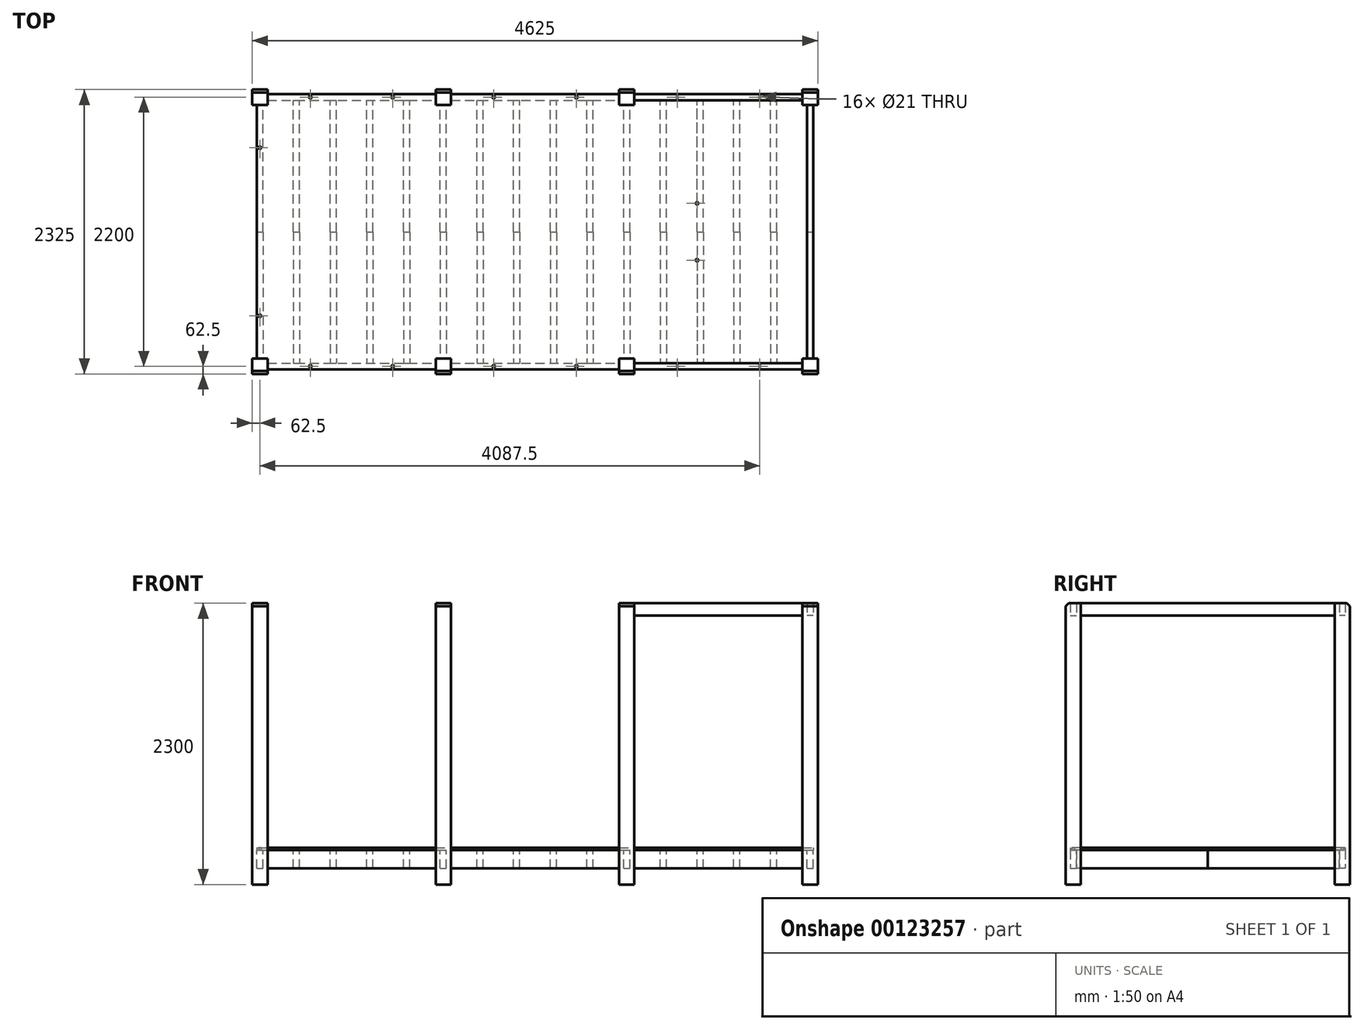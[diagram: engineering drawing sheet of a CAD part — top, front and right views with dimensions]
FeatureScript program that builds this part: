
annotation { "Feature Type Name" : "Feature", "Feature Type Description" : "" }
export const myFeature = defineFeature(function(context is Context, id is Id, definition is map)
    precondition{}
    {
        {
            var Q0;
            Q0=qCreatedBy(makeId("Front.planeOp"),FACE);
            cPlane(context, id + "F0", {"entities" : qUnion([Q0]), "cplaneType" : CPlaneType.OFFSET, "offset" : 1100 * mm, "width" : 150 * mm, "height" : 150 * mm});
        }
        {
            var Q0;
            Q0=qCreatedBy(id+"F0.planeOp",FACE);
            var sketch = newSketch(context, id + "F1", { "sketchPlane" : qUnion([Q0])});
            skLineSegment(sketch, "E0.bottom", {"start": v(-2312.5, 951.35) * mm, "end": v(-2187.5, 951.35) * mm});
            skLineSegment(sketch, "E0.top", {"start": v(-2312.5, -1348.65) * mm, "end": v(-2187.5, -1348.65) * mm});
            skLineSegment(sketch, "E0.left", {"start": v(-2312.5, 951.35) * mm, "end": v(-2312.5, -1348.65) * mm});
            skLineSegment(sketch, "E0.right", {"start": v(-2187.5, 951.35) * mm, "end": v(-2187.5, -1348.65) * mm});
            skLineSegment(sketch, "E1.direction1", {"start": v(-2312.5, -1348.65) * mm, "end": v(-812.5, -1348.65) * mm, "construction": true});
            skLineSegment(sketch, "E2.1.0.0", {"start": v(-812.5, 951.35) * mm, "end": v(-812.5, -1348.65) * mm});
            skLineSegment(sketch, "E2.1.0.1", {"start": v(-812.5, 951.35) * mm, "end": v(-687.5, 951.35) * mm});
            skLineSegment(sketch, "E2.1.0.2", {"start": v(-687.5, 951.35) * mm, "end": v(-687.5, -1348.65) * mm});
            skLineSegment(sketch, "E2.2.0.0", {"start": v(687.5, 951.35) * mm, "end": v(687.5, -1348.65) * mm});
            skLineSegment(sketch, "E2.2.0.1", {"start": v(687.5, 951.35) * mm, "end": v(812.5, 951.35) * mm});
            skLineSegment(sketch, "E2.2.0.2", {"start": v(812.5, 951.35) * mm, "end": v(812.5, -1348.65) * mm});
            skLineSegment(sketch, "E3.0.3.0", {"start": v(2187.5, 951.35) * mm, "end": v(2187.5, -1348.65) * mm});
            skLineSegment(sketch, "E3.3.3.0", {"start": v(2187.5, 951.35) * mm, "end": v(2312.5, 951.35) * mm});
            skLineSegment(sketch, "E3.6.3.0", {"start": v(2312.5, 951.35) * mm, "end": v(2312.5, -1348.65) * mm});
            skLineSegment(sketch, "E4", {"start": v(-812.5, -1348.65) * mm, "end": v(-687.5, -1348.65) * mm});
            skLineSegment(sketch, "E5", {"start": v(687.5, -1348.65) * mm, "end": v(812.5, -1348.65) * mm});
            skLineSegment(sketch, "E6", {"start": v(2187.5, -1348.65) * mm, "end": v(2312.5, -1348.65) * mm});
            skSolve(sketch);
        }
        {
            var Q0;
            Q0=makeQuery(id+"F1.imprint","IMPRINT",FACE,{"disambiguationData":[TD([[makeQuery(id+"F1.imprint","IMPRINT",EDGE,{"derivedFrom":sQuery(id+"F1.wireOp",EDGE,"E0.bottom")}),-1.0]])]});
            var Q1;
            Q1=makeQuery(id+"F1.imprint","IMPRINT",FACE,{"disambiguationData":[TD([[makeQuery(id+"F1.imprint","IMPRINT",EDGE,{"derivedFrom":sQuery(id+"F1.wireOp",EDGE,"E2.1.0.0")}),1.0]])]});
            var Q2;
            Q2=makeQuery(id+"F1.imprint","IMPRINT",FACE,{"disambiguationData":[TD([[makeQuery(id+"F1.imprint","IMPRINT",EDGE,{"derivedFrom":sQuery(id+"F1.wireOp",EDGE,"E2.2.0.0")}),1.0]])]});
            var Q3;
            Q3=makeQuery(id+"F1.imprint","IMPRINT",FACE,{"disambiguationData":[TD([[makeQuery(id+"F1.imprint","IMPRINT",EDGE,{"derivedFrom":sQuery(id+"F1.wireOp",EDGE,"E3.0.3.0")}),1.0]])]});
            extrude(context, id + "F2", {"entities" : qUnion([Q0, Q1, Q2, Q3]), "endBound" : BoundingType.SYMMETRIC, "depth" : 125 * mm});
        }
        {
            var Q0;
            Q0=qCreatedBy(id+"F0.planeOp",FACE);
            var sketch = newSketch(context, id + "F3", { "sketchPlane" : qUnion([Q0])});
            skLineSegment(sketch, "E7.bottom", {"start": v(-2187.5, -1067.65) * mm, "end": v(-812.5, -1067.65) * mm});
            skLineSegment(sketch, "E7.top", {"start": v(-2187.5, -1217.65) * mm, "end": v(-812.5, -1217.65) * mm});
            skLineSegment(sketch, "E7.left", {"start": v(-2187.5, -1067.65) * mm, "end": v(-2187.5, -1217.65) * mm});
            skLineSegment(sketch, "E7.right", {"start": v(-812.5, -1067.65) * mm, "end": v(-812.5, -1217.65) * mm});
            skSolve(sketch);
        }
        {
            var Q0;
            Q0=qCreatedBy(id+"F0.planeOp",FACE);
            var sketch = newSketch(context, id + "F4", { "sketchPlane" : qUnion([Q0])});
            skLineSegment(sketch, "E8.bottom", {"start": v(812.5, -1067.65) * mm, "end": v(2187.5, -1067.65) * mm});
            skLineSegment(sketch, "E8.top", {"start": v(812.5, -1217.65) * mm, "end": v(2187.5, -1217.65) * mm});
            skLineSegment(sketch, "E8.left", {"start": v(812.5, -1067.65) * mm, "end": v(812.5, -1217.65) * mm});
            skLineSegment(sketch, "E8.right", {"start": v(2187.5, -1067.65) * mm, "end": v(2187.5, -1217.65) * mm});
            skLineSegment(sketch, "E9.bottom", {"start": v(-687.5, -1067.65) * mm, "end": v(687.5, -1067.65) * mm});
            skLineSegment(sketch, "E9.top", {"start": v(-687.5, -1217.65) * mm, "end": v(687.5, -1217.65) * mm});
            skLineSegment(sketch, "E9.left", {"start": v(-687.5, -1067.65) * mm, "end": v(-687.5, -1217.65) * mm});
            skLineSegment(sketch, "E9.right", {"start": v(687.5, -1067.65) * mm, "end": v(687.5, -1217.65) * mm});
            skSolve(sketch);
        }
        {
            var Q0;
            Q0=makeQuery(id+"F3.imprint","IMPRINT",FACE,{"disambiguationData":[TD([[makeQuery(id+"F3.imprint","IMPRINT",EDGE,{"derivedFrom":sQuery(id+"F3.wireOp",EDGE,"E7.bottom")}),-1.0]])]});
            var Q1;
            Q1=makeQuery(id+"F4.imprint","IMPRINT",FACE,{"disambiguationData":[TD([[makeQuery(id+"F4.imprint","IMPRINT",EDGE,{"derivedFrom":sQuery(id+"F4.wireOp",EDGE,"E9.bottom")}),-1.0]])]});
            var Q2;
            Q2=makeQuery(id+"F4.imprint","IMPRINT",FACE,{"disambiguationData":[TD([[makeQuery(id+"F4.imprint","IMPRINT",EDGE,{"derivedFrom":sQuery(id+"F4.wireOp",EDGE,"E8.bottom")}),-1.0]])]});
            extrude(context, id + "F5", {"entities" : qUnion([Q0, Q1, Q2]), "endBound" : BoundingType.SYMMETRIC, "depth" : 50 * mm});
        }
        {
            var Q0;
            Q0=qCreatedBy(makeId("Top.planeOp"),FACE);
            cPlane(context, id + "F6", {"entities" : qUnion([Q0]), "cplaneType" : CPlaneType.OFFSET, "offset" : 1067.65 * mm, "oppositeDirection" : true, "width" : 150 * mm, "height" : 150 * mm});
        }
        {
            var Q0;
            Q0=qCreatedBy(id+"F6.planeOp",FACE);
            var sketch = newSketch(context, id + "F7", { "sketchPlane" : qUnion([Q0])});
            skLineSegment(sketch, "E10.bottom", {"start": v(-2275, 0) * mm, "end": v(-2225, 0) * mm});
            skLineSegment(sketch, "E10.top", {"start": v(-2275, -1037.5) * mm, "end": v(-2225, -1037.5) * mm});
            skLineSegment(sketch, "E10.left", {"start": v(-2275, 0) * mm, "end": v(-2275, -1037.5) * mm});
            skLineSegment(sketch, "E10.right", {"start": v(-2225, 0) * mm, "end": v(-2225, -1037.5) * mm});
            skLineSegment(sketch, "E11.1.0.0", {"start": v(-775, 0) * mm, "end": v(-775, -1037.5) * mm});
            skLineSegment(sketch, "E11.1.0.1", {"start": v(-775, 0) * mm, "end": v(-725, 0) * mm});
            skLineSegment(sketch, "E11.1.0.2", {"start": v(-725, 0) * mm, "end": v(-725, -1037.5) * mm});
            skLineSegment(sketch, "E11.1.0.3", {"start": v(-775, -1037.5) * mm, "end": v(-725, -1037.5) * mm});
            skLineSegment(sketch, "E11.2.0.0", {"start": v(725, 0) * mm, "end": v(725, -1037.5) * mm});
            skLineSegment(sketch, "E11.2.0.1", {"start": v(725, 0) * mm, "end": v(775, 0) * mm});
            skLineSegment(sketch, "E11.2.0.2", {"start": v(775, 0) * mm, "end": v(775, -1037.5) * mm});
            skLineSegment(sketch, "E11.2.0.3", {"start": v(725, -1037.5) * mm, "end": v(775, -1037.5) * mm});
            skLineSegment(sketch, "E11.3.0.0", {"start": v(2225, 0) * mm, "end": v(2225, -1037.5) * mm});
            skLineSegment(sketch, "E11.3.0.1", {"start": v(2225, 0) * mm, "end": v(2275, 0) * mm});
            skLineSegment(sketch, "E11.3.0.2", {"start": v(2275, 0) * mm, "end": v(2275, -1037.5) * mm});
            skLineSegment(sketch, "E11.3.0.3", {"start": v(2225, -1037.5) * mm, "end": v(2275, -1037.5) * mm});
            skLineSegment(sketch, "E11.direction1", {"start": v(-2275, -1037.5) * mm, "end": v(-775, -1037.5) * mm, "construction": true});
            skLineSegment(sketch, "E12.bottom", {"start": v(-1975, 0) * mm, "end": v(-1925, 0) * mm});
            skLineSegment(sketch, "E12.top", {"start": v(-1975, -1075) * mm, "end": v(-1925, -1075) * mm});
            skLineSegment(sketch, "E12.left", {"start": v(-1975, 0) * mm, "end": v(-1975, -1075) * mm});
            skLineSegment(sketch, "E12.right", {"start": v(-1925, 0) * mm, "end": v(-1925, -1075) * mm});
            skLineSegment(sketch, "E13.1.0.0", {"start": v(-1675, 0) * mm, "end": v(-1675, -1075) * mm});
            skLineSegment(sketch, "E13.1.0.1", {"start": v(-1675, 0) * mm, "end": v(-1625, 0) * mm});
            skLineSegment(sketch, "E13.1.0.2", {"start": v(-1625, 0) * mm, "end": v(-1625, -1075) * mm});
            skLineSegment(sketch, "E13.1.0.3", {"start": v(-1675, -1075) * mm, "end": v(-1625, -1075) * mm});
            skLineSegment(sketch, "E13.2.0.0", {"start": v(-1375, 0) * mm, "end": v(-1375, -1075) * mm});
            skLineSegment(sketch, "E13.2.0.1", {"start": v(-1375, 0) * mm, "end": v(-1325, 0) * mm});
            skLineSegment(sketch, "E13.2.0.2", {"start": v(-1325, 0) * mm, "end": v(-1325, -1075) * mm});
            skLineSegment(sketch, "E13.2.0.3", {"start": v(-1375, -1075) * mm, "end": v(-1325, -1075) * mm});
            skLineSegment(sketch, "E13.3.0.0", {"start": v(-1075, 0) * mm, "end": v(-1075, -1075) * mm});
            skLineSegment(sketch, "E13.3.0.1", {"start": v(-1075, 0) * mm, "end": v(-1025, 0) * mm});
            skLineSegment(sketch, "E13.3.0.2", {"start": v(-1025, 0) * mm, "end": v(-1025, -1075) * mm});
            skLineSegment(sketch, "E13.3.0.3", {"start": v(-1075, -1075) * mm, "end": v(-1025, -1075) * mm});
            skLineSegment(sketch, "E13.direction1", {"start": v(-1975, -1075) * mm, "end": v(-1675, -1075) * mm, "construction": true});
            skLineSegment(sketch, "E14.1.0.0", {"start": v(475, 0) * mm, "end": v(475, -1075) * mm});
            skLineSegment(sketch, "E14.1.0.1", {"start": v(-475, 0) * mm, "end": v(-475, -1075) * mm});
            skLineSegment(sketch, "E14.1.0.2", {"start": v(125, 0) * mm, "end": v(125, -1075) * mm});
            skLineSegment(sketch, "E14.1.0.3", {"start": v(-175, 0) * mm, "end": v(-175, -1075) * mm});
            skLineSegment(sketch, "E14.1.0.4", {"start": v(-475, -1075) * mm, "end": v(-175, -1075) * mm, "construction": true});
            skLineSegment(sketch, "E14.1.0.5", {"start": v(-125, 0) * mm, "end": v(-125, -1075) * mm});
            skLineSegment(sketch, "E14.1.0.6", {"start": v(-425, 0) * mm, "end": v(-425, -1075) * mm});
            skLineSegment(sketch, "E14.1.0.7", {"start": v(425, 0) * mm, "end": v(425, -1075) * mm});
            skLineSegment(sketch, "E14.1.0.8", {"start": v(175, 0) * mm, "end": v(175, -1075) * mm});
            skLineSegment(sketch, "E14.1.0.9", {"start": v(-475, -1075) * mm, "end": v(-425, -1075) * mm});
            skLineSegment(sketch, "E14.1.0.10", {"start": v(-175, 0) * mm, "end": v(-125, 0) * mm});
            skLineSegment(sketch, "E14.1.0.11", {"start": v(125, 0) * mm, "end": v(175, 0) * mm});
            skLineSegment(sketch, "E14.1.0.12", {"start": v(425, 0) * mm, "end": v(475, 0) * mm});
            skLineSegment(sketch, "E14.1.0.13", {"start": v(125, -1075) * mm, "end": v(175, -1075) * mm});
            skLineSegment(sketch, "E14.1.0.14", {"start": v(-475, 0) * mm, "end": v(-425, 0) * mm});
            skLineSegment(sketch, "E14.1.0.15", {"start": v(425, -1075) * mm, "end": v(475, -1075) * mm});
            skLineSegment(sketch, "E14.1.0.16", {"start": v(-175, -1075) * mm, "end": v(-125, -1075) * mm});
            skLineSegment(sketch, "E14.2.0.0", {"start": v(1975, 0) * mm, "end": v(1975, -1075) * mm});
            skLineSegment(sketch, "E14.2.0.1", {"start": v(1025, 0) * mm, "end": v(1025, -1075) * mm});
            skLineSegment(sketch, "E14.2.0.2", {"start": v(1625, 0) * mm, "end": v(1625, -1075) * mm});
            skLineSegment(sketch, "E14.2.0.3", {"start": v(1325, 0) * mm, "end": v(1325, -1075) * mm});
            skLineSegment(sketch, "E14.2.0.4", {"start": v(1025, -1075) * mm, "end": v(1325, -1075) * mm, "construction": true});
            skLineSegment(sketch, "E14.2.0.5", {"start": v(1375, 0) * mm, "end": v(1375, -1075) * mm});
            skLineSegment(sketch, "E14.2.0.6", {"start": v(1075, 0) * mm, "end": v(1075, -1075) * mm});
            skLineSegment(sketch, "E14.2.0.7", {"start": v(1925, 0) * mm, "end": v(1925, -1075) * mm});
            skLineSegment(sketch, "E14.2.0.8", {"start": v(1675, 0) * mm, "end": v(1675, -1075) * mm});
            skLineSegment(sketch, "E14.2.0.9", {"start": v(1025, -1075) * mm, "end": v(1075, -1075) * mm});
            skLineSegment(sketch, "E14.2.0.10", {"start": v(1325, 0) * mm, "end": v(1375, 0) * mm});
            skLineSegment(sketch, "E14.2.0.11", {"start": v(1625, 0) * mm, "end": v(1675, 0) * mm});
            skLineSegment(sketch, "E14.2.0.12", {"start": v(1925, 0) * mm, "end": v(1975, 0) * mm});
            skLineSegment(sketch, "E14.2.0.13", {"start": v(1625, -1075) * mm, "end": v(1675, -1075) * mm});
            skLineSegment(sketch, "E14.2.0.14", {"start": v(1025, 0) * mm, "end": v(1075, 0) * mm});
            skLineSegment(sketch, "E14.2.0.15", {"start": v(1925, -1075) * mm, "end": v(1975, -1075) * mm});
            skLineSegment(sketch, "E14.2.0.16", {"start": v(1325, -1075) * mm, "end": v(1375, -1075) * mm});
            skLineSegment(sketch, "E14.direction1", {"start": v(-1975, -1075) * mm, "end": v(-475, -1075) * mm, "construction": true});
            skSolve(sketch);
        }
        {
            var Q0;
            Q0=makeQuery(id+"F7.imprint","IMPRINT",FACE,{"disambiguationData":[TD([[makeQuery(id+"F7.imprint","IMPRINT",EDGE,{"derivedFrom":sQuery(id+"F7.wireOp",EDGE,"E10.bottom")}),-1.0]])]});
            var Q1;
            Q1=makeQuery(id+"F7.imprint","IMPRINT",FACE,{"disambiguationData":[TD([[makeQuery(id+"F7.imprint","IMPRINT",EDGE,{"derivedFrom":sQuery(id+"F7.wireOp",EDGE,"E12.bottom")}),-1.0]])]});
            var Q2;
            Q2=makeQuery(id+"F7.imprint","IMPRINT",FACE,{"disambiguationData":[TD([[makeQuery(id+"F7.imprint","IMPRINT",EDGE,{"derivedFrom":sQuery(id+"F7.wireOp",EDGE,"E13.1.0.0")}),1.0]])]});
            var Q3;
            Q3=makeQuery(id+"F7.imprint","IMPRINT",FACE,{"disambiguationData":[TD([[makeQuery(id+"F7.imprint","IMPRINT",EDGE,{"derivedFrom":sQuery(id+"F7.wireOp",EDGE,"E13.2.0.0")}),1.0]])]});
            var Q4;
            Q4=makeQuery(id+"F7.imprint","IMPRINT",FACE,{"disambiguationData":[TD([[makeQuery(id+"F7.imprint","IMPRINT",EDGE,{"derivedFrom":sQuery(id+"F7.wireOp",EDGE,"E13.3.0.0")}),1.0]])]});
            var Q5;
            Q5=makeQuery(id+"F7.imprint","IMPRINT",FACE,{"disambiguationData":[TD([[makeQuery(id+"F7.imprint","IMPRINT",EDGE,{"derivedFrom":sQuery(id+"F7.wireOp",EDGE,"E11.1.0.0")}),1.0]])]});
            var Q6;
            Q6=makeQuery(id+"F7.imprint","IMPRINT",FACE,{"disambiguationData":[TD([[makeQuery(id+"F7.imprint","IMPRINT",EDGE,{"derivedFrom":sQuery(id+"F7.wireOp",EDGE,"E14.1.0.1")}),1.0]])]});
            var Q7;
            Q7=makeQuery(id+"F7.imprint","IMPRINT",FACE,{"disambiguationData":[TD([[makeQuery(id+"F7.imprint","IMPRINT",EDGE,{"derivedFrom":sQuery(id+"F7.wireOp",EDGE,"E14.1.0.3")}),1.0]])]});
            var Q8;
            Q8=makeQuery(id+"F7.imprint","IMPRINT",FACE,{"disambiguationData":[TD([[makeQuery(id+"F7.imprint","IMPRINT",EDGE,{"derivedFrom":sQuery(id+"F7.wireOp",EDGE,"E14.1.0.2")}),1.0]])]});
            var Q9;
            Q9=makeQuery(id+"F7.imprint","IMPRINT",FACE,{"disambiguationData":[TD([[makeQuery(id+"F7.imprint","IMPRINT",EDGE,{"derivedFrom":sQuery(id+"F7.wireOp",EDGE,"E14.1.0.0")}),-1.0]])]});
            var Q10;
            Q10=makeQuery(id+"F7.imprint","IMPRINT",FACE,{"disambiguationData":[TD([[makeQuery(id+"F7.imprint","IMPRINT",EDGE,{"derivedFrom":sQuery(id+"F7.wireOp",EDGE,"E11.2.0.0")}),1.0]])]});
            var Q11;
            Q11=makeQuery(id+"F7.imprint","IMPRINT",FACE,{"disambiguationData":[TD([[makeQuery(id+"F7.imprint","IMPRINT",EDGE,{"derivedFrom":sQuery(id+"F7.wireOp",EDGE,"E14.2.0.1")}),1.0]])]});
            var Q12;
            Q12=makeQuery(id+"F7.imprint","IMPRINT",FACE,{"disambiguationData":[TD([[makeQuery(id+"F7.imprint","IMPRINT",EDGE,{"derivedFrom":sQuery(id+"F7.wireOp",EDGE,"E14.2.0.3")}),1.0]])]});
            var Q13;
            Q13=makeQuery(id+"F7.imprint","IMPRINT",FACE,{"disambiguationData":[TD([[makeQuery(id+"F7.imprint","IMPRINT",EDGE,{"derivedFrom":sQuery(id+"F7.wireOp",EDGE,"E14.2.0.2")}),1.0]])]});
            var Q14;
            Q14=makeQuery(id+"F7.imprint","IMPRINT",FACE,{"disambiguationData":[TD([[makeQuery(id+"F7.imprint","IMPRINT",EDGE,{"derivedFrom":sQuery(id+"F7.wireOp",EDGE,"E14.2.0.0")}),-1.0]])]});
            var Q15;
            Q15=makeQuery(id+"F7.imprint","IMPRINT",FACE,{"disambiguationData":[TD([[makeQuery(id+"F7.imprint","IMPRINT",EDGE,{"derivedFrom":sQuery(id+"F7.wireOp",EDGE,"E11.3.0.0")}),1.0]])]});
            extrude(context, id + "F8", {"entities" : qUnion([Q0, Q1, Q2, Q3, Q4, Q5, Q6, Q7, Q8, Q9, Q10, Q11, Q12, Q13, Q14, Q15]), "oppositeDirection" : true, "depth" : 150 * mm});
        }
        {
            var Q0;
            Q0=makeQuery(id+"F2.opExtrude","SWEPT_BODY",BODY,{"disambiguationData":[OSD([sQuery(id+"F1.wireOp",EDGE,"E0.bottom"),sQuery(id+"F1.wireOp",EDGE,"E0.top"),sQuery(id+"F1.wireOp",EDGE,"E0.left"),sQuery(id+"F1.wireOp",EDGE,"E0.right")])]});
            var Q1;
            Q1=makeQuery(id+"F5.opExtrude","SWEPT_BODY",BODY,{"disambiguationData":[OSD([sQuery(id+"F3.wireOp",EDGE,"E7.bottom"),sQuery(id+"F3.wireOp",EDGE,"E7.top"),sQuery(id+"F3.wireOp",EDGE,"E7.left"),sQuery(id+"F3.wireOp",EDGE,"E7.right")])]});
            var Q2;
            Q2=makeQuery(id+"F2.opExtrude","SWEPT_BODY",BODY,{"disambiguationData":[OSD([sQuery(id+"F1.wireOp",EDGE,"E3.0.3.0"),sQuery(id+"F1.wireOp",EDGE,"E3.3.3.0"),sQuery(id+"F1.wireOp",EDGE,"E3.6.3.0"),sQuery(id+"F1.wireOp",EDGE,"E6")])]});
            var Q3;
            Q3=makeQuery(id+"F2.opExtrude","SWEPT_BODY",BODY,{"disambiguationData":[OSD([sQuery(id+"F1.wireOp",EDGE,"E2.1.0.0"),sQuery(id+"F1.wireOp",EDGE,"E2.1.0.1"),sQuery(id+"F1.wireOp",EDGE,"E2.1.0.2"),sQuery(id+"F1.wireOp",EDGE,"E4")])]});
            var Q4;
            Q4=makeQuery(id+"F5.opExtrude","SWEPT_BODY",BODY,{"disambiguationData":[OSD([sQuery(id+"F4.wireOp",EDGE,"E8.bottom"),sQuery(id+"F4.wireOp",EDGE,"E8.top"),sQuery(id+"F4.wireOp",EDGE,"E8.left"),sQuery(id+"F4.wireOp",EDGE,"E8.right")])]});
            var Q5;
            Q5=makeQuery(id+"F5.opExtrude","SWEPT_BODY",BODY,{"disambiguationData":[OSD([sQuery(id+"F4.wireOp",EDGE,"E9.bottom"),sQuery(id+"F4.wireOp",EDGE,"E9.top"),sQuery(id+"F4.wireOp",EDGE,"E9.left"),sQuery(id+"F4.wireOp",EDGE,"E9.right")])]});
            var Q6;
            Q6=makeQuery(id+"F2.opExtrude","SWEPT_BODY",BODY,{"disambiguationData":[OSD([sQuery(id+"F1.wireOp",EDGE,"E2.2.0.0"),sQuery(id+"F1.wireOp",EDGE,"E2.2.0.1"),sQuery(id+"F1.wireOp",EDGE,"E2.2.0.2"),sQuery(id+"F1.wireOp",EDGE,"E5")])]});
            var Q7;
            Q7=makeQuery(id+"F8.opExtrude","SWEPT_BODY",BODY,{"disambiguationData":[OSD([sQuery(id+"F7.wireOp",EDGE,"E14.2.0.3"),sQuery(id+"F7.wireOp",EDGE,"E14.2.0.5"),sQuery(id+"F7.wireOp",EDGE,"E14.2.0.10"),sQuery(id+"F7.wireOp",EDGE,"E14.2.0.16")])]});
            var Q8;
            Q8=makeQuery(id+"F8.opExtrude","SWEPT_BODY",BODY,{"disambiguationData":[OSD([sQuery(id+"F7.wireOp",EDGE,"E14.2.0.2"),sQuery(id+"F7.wireOp",EDGE,"E14.2.0.8"),sQuery(id+"F7.wireOp",EDGE,"E14.2.0.11"),sQuery(id+"F7.wireOp",EDGE,"E14.2.0.13")])]});
            var Q9;
            Q9=makeQuery(id+"F8.opExtrude","SWEPT_BODY",BODY,{"disambiguationData":[OSD([sQuery(id+"F7.wireOp",EDGE,"E14.2.0.1"),sQuery(id+"F7.wireOp",EDGE,"E14.2.0.6"),sQuery(id+"F7.wireOp",EDGE,"E14.2.0.9"),sQuery(id+"F7.wireOp",EDGE,"E14.2.0.14")])]});
            var Q10;
            Q10=makeQuery(id+"F8.opExtrude","SWEPT_BODY",BODY,{"disambiguationData":[OSD([sQuery(id+"F7.wireOp",EDGE,"E14.2.0.0"),sQuery(id+"F7.wireOp",EDGE,"E14.2.0.7"),sQuery(id+"F7.wireOp",EDGE,"E14.2.0.12"),sQuery(id+"F7.wireOp",EDGE,"E14.2.0.15")])]});
            var Q11;
            Q11=makeQuery(id+"F8.opExtrude","SWEPT_BODY",BODY,{"disambiguationData":[OSD([sQuery(id+"F7.wireOp",EDGE,"E14.1.0.3"),sQuery(id+"F7.wireOp",EDGE,"E14.1.0.5"),sQuery(id+"F7.wireOp",EDGE,"E14.1.0.10"),sQuery(id+"F7.wireOp",EDGE,"E14.1.0.16")])]});
            var Q12;
            Q12=makeQuery(id+"F8.opExtrude","SWEPT_BODY",BODY,{"disambiguationData":[OSD([sQuery(id+"F7.wireOp",EDGE,"E14.1.0.2"),sQuery(id+"F7.wireOp",EDGE,"E14.1.0.8"),sQuery(id+"F7.wireOp",EDGE,"E14.1.0.11"),sQuery(id+"F7.wireOp",EDGE,"E14.1.0.13")])]});
            var Q13;
            Q13=makeQuery(id+"F8.opExtrude","SWEPT_BODY",BODY,{"disambiguationData":[OSD([sQuery(id+"F7.wireOp",EDGE,"E14.1.0.1"),sQuery(id+"F7.wireOp",EDGE,"E14.1.0.6"),sQuery(id+"F7.wireOp",EDGE,"E14.1.0.9"),sQuery(id+"F7.wireOp",EDGE,"E14.1.0.14")])]});
            var Q14;
            Q14=makeQuery(id+"F8.opExtrude","SWEPT_BODY",BODY,{"disambiguationData":[OSD([sQuery(id+"F7.wireOp",EDGE,"E14.1.0.0"),sQuery(id+"F7.wireOp",EDGE,"E14.1.0.7"),sQuery(id+"F7.wireOp",EDGE,"E14.1.0.12"),sQuery(id+"F7.wireOp",EDGE,"E14.1.0.15")])]});
            var Q15;
            Q15=makeQuery(id+"F8.opExtrude","SWEPT_BODY",BODY,{"disambiguationData":[OSD([sQuery(id+"F7.wireOp",EDGE,"E13.3.0.0"),sQuery(id+"F7.wireOp",EDGE,"E13.3.0.1"),sQuery(id+"F7.wireOp",EDGE,"E13.3.0.2"),sQuery(id+"F7.wireOp",EDGE,"E13.3.0.3")])]});
            var Q16;
            Q16=makeQuery(id+"F8.opExtrude","SWEPT_BODY",BODY,{"disambiguationData":[OSD([sQuery(id+"F7.wireOp",EDGE,"E13.1.0.0"),sQuery(id+"F7.wireOp",EDGE,"E13.1.0.1"),sQuery(id+"F7.wireOp",EDGE,"E13.1.0.2"),sQuery(id+"F7.wireOp",EDGE,"E13.1.0.3")])]});
            var Q17;
            Q17=makeQuery(id+"F8.opExtrude","SWEPT_BODY",BODY,{"disambiguationData":[OSD([sQuery(id+"F7.wireOp",EDGE,"E13.2.0.0"),sQuery(id+"F7.wireOp",EDGE,"E13.2.0.1"),sQuery(id+"F7.wireOp",EDGE,"E13.2.0.2"),sQuery(id+"F7.wireOp",EDGE,"E13.2.0.3")])]});
            var Q18;
            Q18=makeQuery(id+"F8.opExtrude","SWEPT_BODY",BODY,{"disambiguationData":[OSD([sQuery(id+"F7.wireOp",EDGE,"E10.bottom"),sQuery(id+"F7.wireOp",EDGE,"E10.top"),sQuery(id+"F7.wireOp",EDGE,"E10.left"),sQuery(id+"F7.wireOp",EDGE,"E10.right")])]});
            var Q19;
            Q19=makeQuery(id+"F8.opExtrude","SWEPT_BODY",BODY,{"disambiguationData":[OSD([sQuery(id+"F7.wireOp",EDGE,"E12.bottom"),sQuery(id+"F7.wireOp",EDGE,"E12.top"),sQuery(id+"F7.wireOp",EDGE,"E12.left"),sQuery(id+"F7.wireOp",EDGE,"E12.right")])]});
            var Q20;
            Q20=makeQuery(id+"F8.opExtrude","SWEPT_BODY",BODY,{"disambiguationData":[OSD([sQuery(id+"F7.wireOp",EDGE,"E11.3.0.0"),sQuery(id+"F7.wireOp",EDGE,"E11.3.0.1"),sQuery(id+"F7.wireOp",EDGE,"E11.3.0.2"),sQuery(id+"F7.wireOp",EDGE,"E11.3.0.3")])]});
            var Q21;
            Q21=makeQuery(id+"F8.opExtrude","SWEPT_BODY",BODY,{"disambiguationData":[OSD([sQuery(id+"F7.wireOp",EDGE,"E11.1.0.0"),sQuery(id+"F7.wireOp",EDGE,"E11.1.0.1"),sQuery(id+"F7.wireOp",EDGE,"E11.1.0.2"),sQuery(id+"F7.wireOp",EDGE,"E11.1.0.3")])]});
            var Q22;
            Q22=makeQuery(id+"F8.opExtrude","SWEPT_BODY",BODY,{"disambiguationData":[OSD([sQuery(id+"F7.wireOp",EDGE,"E11.2.0.0"),sQuery(id+"F7.wireOp",EDGE,"E11.2.0.1"),sQuery(id+"F7.wireOp",EDGE,"E11.2.0.2"),sQuery(id+"F7.wireOp",EDGE,"E11.2.0.3")])]});
            var Q23;
            Q23=qCreatedBy(makeId("Front.planeOp"),FACE);
            mirror(context, id + "F9", {"entities" : qUnion([Q0, Q1, Q2, Q3, Q4, Q5, Q6, Q7, Q8, Q9, Q10, Q11, Q12, Q13, Q14, Q15, Q16, Q17, Q18, Q19, Q20, Q21, Q22]), "mirrorPlane" : qUnion([Q23])});
        }
        {
            var Q0;
            Q0=qCreatedBy(id+"F6.planeOp",FACE);
            var sketch = newSketch(context, id + "F10", { "sketchPlane" : qUnion([Q0])});
            skLineSegment(sketch, "E15.bottom", {"start": v(-2187.5, -1037.5) * mm, "end": v(-812.5, -1037.5) * mm});
            skLineSegment(sketch, "E15.top", {"start": v(-2187.5, -1125) * mm, "end": v(-812.5, -1125) * mm});
            skLineSegment(sketch, "E15.left", {"start": v(-2187.5, -1037.5) * mm, "end": v(-2187.5, -1125) * mm});
            skLineSegment(sketch, "E15.right", {"start": v(-812.5, -1037.5) * mm, "end": v(-812.5, -1125) * mm});
            skLineSegment(sketch, "E16.1.0.0", {"start": v(-687.5, -1037.5) * mm, "end": v(687.5, -1037.5) * mm});
            skLineSegment(sketch, "E16.1.0.1", {"start": v(-687.5, -1125) * mm, "end": v(687.5, -1125) * mm});
            skLineSegment(sketch, "E16.1.0.2", {"start": v(687.5, -1037.5) * mm, "end": v(687.5, -1125) * mm});
            skLineSegment(sketch, "E16.1.0.3", {"start": v(-687.5, -1037.5) * mm, "end": v(-687.5, -1125) * mm});
            skLineSegment(sketch, "E16.2.0.0", {"start": v(812.5, -1037.5) * mm, "end": v(2187.5, -1037.5) * mm});
            skLineSegment(sketch, "E16.2.0.1", {"start": v(812.5, -1125) * mm, "end": v(2187.5, -1125) * mm});
            skLineSegment(sketch, "E16.2.0.2", {"start": v(2187.5, -1037.5) * mm, "end": v(2187.5, -1125) * mm});
            skLineSegment(sketch, "E16.2.0.3", {"start": v(812.5, -1037.5) * mm, "end": v(812.5, -1125) * mm});
            skLineSegment(sketch, "E16.direction1", {"start": v(-2187.5, -1125) * mm, "end": v(-687.5, -1125) * mm, "construction": true});
            skCircle(sketch, "E17", {"center": v(-1837.5, -1100) * mm, "radius": 10.5 * mm});
            skCircle(sketch, "E18", {"center": v(-1162.5, -1100) * mm, "radius": 10.5 * mm});
            skCircle(sketch, "E19.1.0.0", {"center": v(-337.5, -1100) * mm, "radius": 10.5 * mm});
            skCircle(sketch, "E19.2.0.0", {"center": v(1162.5, -1100) * mm, "radius": 10.5 * mm});
            skLineSegment(sketch, "E19.direction1", {"start": v(-1837.5, -1100) * mm, "end": v(-337.5, -1100) * mm, "construction": true});
            skCircle(sketch, "E20.1.0.0", {"center": v(337.5, -1100) * mm, "radius": 10.5 * mm});
            skCircle(sketch, "E20.2.0.0", {"center": v(1837.5, -1100) * mm, "radius": 10.5 * mm});
            skLineSegment(sketch, "E20.direction1", {"start": v(-1162.5, -1100) * mm, "end": v(337.5, -1100) * mm, "construction": true});
            skLineSegment(sketch, "E21.top", {"start": v(-2275, -1037.5) * mm, "end": v(2275, -1037.5) * mm});
            skLineSegment(sketch, "E21.left", {"start": v(-2275, 1037.5) * mm, "end": v(-2275, -1037.5) * mm});
            skLineSegment(sketch, "E21.right", {"start": v(2275, 1037.5) * mm, "end": v(2275, -1037.5) * mm});
            skLineSegment(sketch, "E22", {"start": v(-2275, 1037.5) * mm, "end": v(2275, 1037.5) * mm});
            skLineSegment(sketch, "E23.bottom", {"start": v(-2187.5, 1125) * mm, "end": v(-812.5, 1125) * mm});
            skLineSegment(sketch, "E23.top", {"start": v(-2187.5, 1037.5) * mm, "end": v(-812.5, 1037.5) * mm});
            skLineSegment(sketch, "E23.left", {"start": v(-2187.5, 1125) * mm, "end": v(-2187.5, 1037.5) * mm});
            skLineSegment(sketch, "E23.right", {"start": v(-812.5, 1125) * mm, "end": v(-812.5, 1037.5) * mm});
            skLineSegment(sketch, "E24.bottom", {"start": v(-687.5, 1125) * mm, "end": v(687.5, 1125) * mm});
            skLineSegment(sketch, "E24.top", {"start": v(-687.5, 1037.5) * mm, "end": v(687.5, 1037.5) * mm});
            skLineSegment(sketch, "E24.left", {"start": v(-687.5, 1125) * mm, "end": v(-687.5, 1037.5) * mm});
            skLineSegment(sketch, "E24.right", {"start": v(687.5, 1125) * mm, "end": v(687.5, 1037.5) * mm});
            skLineSegment(sketch, "E25.bottom", {"start": v(812.5, 1125) * mm, "end": v(2187.5, 1125) * mm});
            skLineSegment(sketch, "E25.top", {"start": v(812.5, 1037.5) * mm, "end": v(2187.5, 1037.5) * mm});
            skLineSegment(sketch, "E25.left", {"start": v(812.5, 1125) * mm, "end": v(812.5, 1037.5) * mm});
            skLineSegment(sketch, "E25.right", {"start": v(2187.5, 1125) * mm, "end": v(2187.5, 1037.5) * mm});
            skCircle(sketch, "E26.MirrorC", {"center": v(-1837.5, 1100) * mm, "radius": 10.5 * mm});
            skCircle(sketch, "E27.MirrorC", {"center": v(-1162.5, 1100) * mm, "radius": 10.5 * mm});
            skCircle(sketch, "E28.MirrorC", {"center": v(-337.5, 1100) * mm, "radius": 10.5 * mm});
            skCircle(sketch, "E29.MirrorC", {"center": v(337.5, 1100) * mm, "radius": 10.5 * mm});
            skCircle(sketch, "E30.MirrorC", {"center": v(1162.5, 1100) * mm, "radius": 10.5 * mm});
            skCircle(sketch, "E31.MirrorC", {"center": v(1837.5, 1100) * mm, "radius": 10.5 * mm});
            skCircle(sketch, "E32", {"center": v(-2250, 687.5) * mm, "radius": 10.5 * mm});
            skCircle(sketch, "E33.MirrorC", {"center": v(-2250, -687.5) * mm, "radius": 10.5 * mm});
            skCircle(sketch, "E34", {"center": v(1325, 232.5) * mm, "radius": 10.5 * mm});
            skCircle(sketch, "E35.MirrorC", {"center": v(1325, -232.5) * mm, "radius": 10.5 * mm});
            skSolve(sketch);
        }
        {
            var Q0;
            Q0=makeQuery(id+"F10.imprint","IMPRINT",FACE,{"disambiguationData":[TD([[makeQuery(id+"F10.imprint","IMPRINT",EDGE,{"derivedFrom":sQuery(id+"F10.wireOp",EDGE,"E23.bottom")}),-1.0]])]});
            var Q1;
            Q1=makeQuery(id+"F10.imprint","IMPRINT",FACE,{"disambiguationData":[TD([[makeQuery(id+"F10.imprint","IMPRINT",EDGE,{"derivedFrom":sQuery(id+"F10.wireOp",EDGE,"E24.bottom")}),-1.0]])]});
            var Q2;
            Q2=makeQuery(id+"F10.imprint","IMPRINT",FACE,{"disambiguationData":[TD([[makeQuery(id+"F10.imprint","IMPRINT",EDGE,{"derivedFrom":sQuery(id+"F10.wireOp",EDGE,"E25.bottom")}),-1.0]])]});
            var Q3;
            {var subQ1=sQuery(id+"F10.wireOp",EDGE,"E21.left");Q3=makeQuery(id+"F10.imprint","IMPRINT",FACE,{"disambiguationData":[TD([[makeQuery(id+"F10.imprint","IMPRINT",EDGE,{"derivedFrom":subQ1}),1.0]])]});}
            var Q4;
            Q4=makeQuery(id+"F10.imprint","IMPRINT",FACE,{"disambiguationData":[TD([[makeQuery(id+"F10.imprint","IMPRINT",EDGE,{"derivedFrom":sQuery(id+"F10.wireOp",EDGE,"E19.2.0.0")}),-1.0]])]});
            var Q5;
            Q5=makeQuery(id+"F10.imprint","IMPRINT",FACE,{"disambiguationData":[TD([[makeQuery(id+"F10.imprint","IMPRINT",EDGE,{"derivedFrom":sQuery(id+"F10.wireOp",EDGE,"E16.1.0.3")}),1.0]])]});
            var Q6;
            Q6=makeQuery(id+"F10.imprint","IMPRINT",FACE,{"disambiguationData":[TD([[makeQuery(id+"F10.imprint","IMPRINT",EDGE,{"derivedFrom":sQuery(id+"F10.wireOp",EDGE,"E15.top")}),1.0]])]});
            extrude(context, id + "F11", {"entities" : qUnion([Q0, Q1, Q2, Q3, Q4, Q5, Q6]), "depth" : 19 * mm});
        }
        {
            var Q0;
            Q0=qCreatedBy(id+"F0.planeOp",FACE);
            var sketch = newSketch(context, id + "F12", { "sketchPlane" : qUnion([Q0])});
            skLineSegment(sketch, "E36.bottom", {"start": v(812.5, 951.35) * mm, "end": v(2187.5, 951.35) * mm});
            skLineSegment(sketch, "E36.top", {"start": v(812.5, 851.35) * mm, "end": v(2187.5, 851.35) * mm});
            skLineSegment(sketch, "E36.left", {"start": v(812.5, 951.35) * mm, "end": v(812.5, 851.35) * mm});
            skLineSegment(sketch, "E36.right", {"start": v(2187.5, 951.35) * mm, "end": v(2187.5, 851.35) * mm});
            skSolve(sketch);
        }
        {
            var Q0;
            Q0=makeQuery(id+"F12.imprint","IMPRINT",FACE,{"disambiguationData":[TD([[makeQuery(id+"F12.imprint","IMPRINT",EDGE,{"derivedFrom":sQuery(id+"F12.wireOp",EDGE,"E36.bottom")}),-1.0]])]});
            extrude(context, id + "F13", {"entities" : qUnion([Q0]), "endBound" : BoundingType.SYMMETRIC, "depth" : 50 * mm});
        }
        {
            var Q0;
            Q0=makeQuery(id+"F13.opExtrude","SWEPT_BODY",BODY,{"disambiguationData":[OSD([sQuery(id+"F12.wireOp",EDGE,"E36.bottom"),sQuery(id+"F12.wireOp",EDGE,"E36.top"),sQuery(id+"F12.wireOp",EDGE,"E36.left"),sQuery(id+"F12.wireOp",EDGE,"E36.right")])]});
            var Q1;
            Q1=qCreatedBy(makeId("Front.planeOp"),FACE);
            mirror(context, id + "F14", {"entities" : qUnion([Q0]), "mirrorPlane" : qUnion([Q1])});
        }
        {
            var Q0;
            Q0=qCreatedBy(makeId("Right.planeOp"),FACE);
            cPlane(context, id + "F15", {"entities" : qUnion([Q0]), "cplaneType" : CPlaneType.OFFSET, "offset" : 2250 * mm, "width" : 150 * mm, "height" : 150 * mm});
        }
        {
            var Q0;
            Q0=qCreatedBy(id+"F15.planeOp",FACE);
            var sketch = newSketch(context, id + "F16", { "sketchPlane" : qUnion([Q0])});
            skLineSegment(sketch, "E37.bottom", {"start": v(-1037.5, 951.35) * mm, "end": v(1037.5, 951.35) * mm});
            skLineSegment(sketch, "E37.top", {"start": v(-1037.5, 851.35) * mm, "end": v(1037.5, 851.35) * mm});
            skLineSegment(sketch, "E37.left", {"start": v(-1037.5, 951.35) * mm, "end": v(-1037.5, 851.35) * mm});
            skLineSegment(sketch, "E37.right", {"start": v(1037.5, 951.35) * mm, "end": v(1037.5, 851.35) * mm});
            skSolve(sketch);
        }
        {
            var Q0;
            Q0=makeQuery(id+"F16.imprint","IMPRINT",FACE,{"disambiguationData":[TD([[makeQuery(id+"F16.imprint","IMPRINT",EDGE,{"derivedFrom":sQuery(id+"F16.wireOp",EDGE,"E37.bottom")}),-1.0]])]});
            extrude(context, id + "F17", {"entities" : qUnion([Q0]), "endBound" : BoundingType.SYMMETRIC, "depth" : 50 * mm});
        }
        {
            var Q0;
            Q0=qCreatedBy(id+"F15.planeOp",FACE);
            var sketch = newSketch(context, id + "F18", { "sketchPlane" : qUnion([Q0])});
            skLineSegment(sketch, "E38", {"start": v(-1162.5, 951.35) * mm, "end": v(-1137, 951.35) * mm});
            skLineSegment(sketch, "E39", {"start": v(-1137, 951.35) * mm, "end": v(-1162.5, 925.85) * mm});
            skLineSegment(sketch, "E40", {"start": v(-1162.5, 925.85) * mm, "end": v(-1162.5, 951.35) * mm});
            skLineSegment(sketch, "E41.MirrorCS", {"start": v(1162.5, 951.35) * mm, "end": v(1137, 951.35) * mm});
            skLineSegment(sketch, "E42.MirrorCS", {"start": v(1137, 951.35) * mm, "end": v(1162.5, 925.85) * mm});
            skLineSegment(sketch, "E43.MirrorCS", {"start": v(1162.5, 925.85) * mm, "end": v(1162.5, 951.35) * mm});
            skSolve(sketch);
        }
        {
            var Q0;
            Q0 = qSketchRegion(id + "F18", true);
            var Q1;
            Q1=makeQuery(id+"F2.opExtrude","SWEPT_FACE",FACE,{"disambiguationData":[OSD([sQuery(id+"F1.wireOp",EDGE,"E3.6.3.0")])]});
            var Q2;
            Q2=makeQuery(id+"F2.opExtrude","SWEPT_FACE",FACE,{"disambiguationData":[OSD([sQuery(id+"F1.wireOp",EDGE,"E0.left")])]});
            extrude(context, id + "F19", {"entities" : qUnion([Q0]), "operationType" : NewBodyOperationType.REMOVE, "endBound" : BoundingType.UP_TO_SURFACE, "endBoundEntityFace" : qUnion([Q1]), "depth" : 25 * mm, "hasSecondDirection" : true, "secondDirectionBound" : SecondDirectionBoundingType.THROUGH_ALL, "secondDirectionOppositeDirection" : true, "secondDirectionBoundEntityFace" : qUnion([Q2]), "secondDirectionDepth" : 25 * mm});
        }
    });
